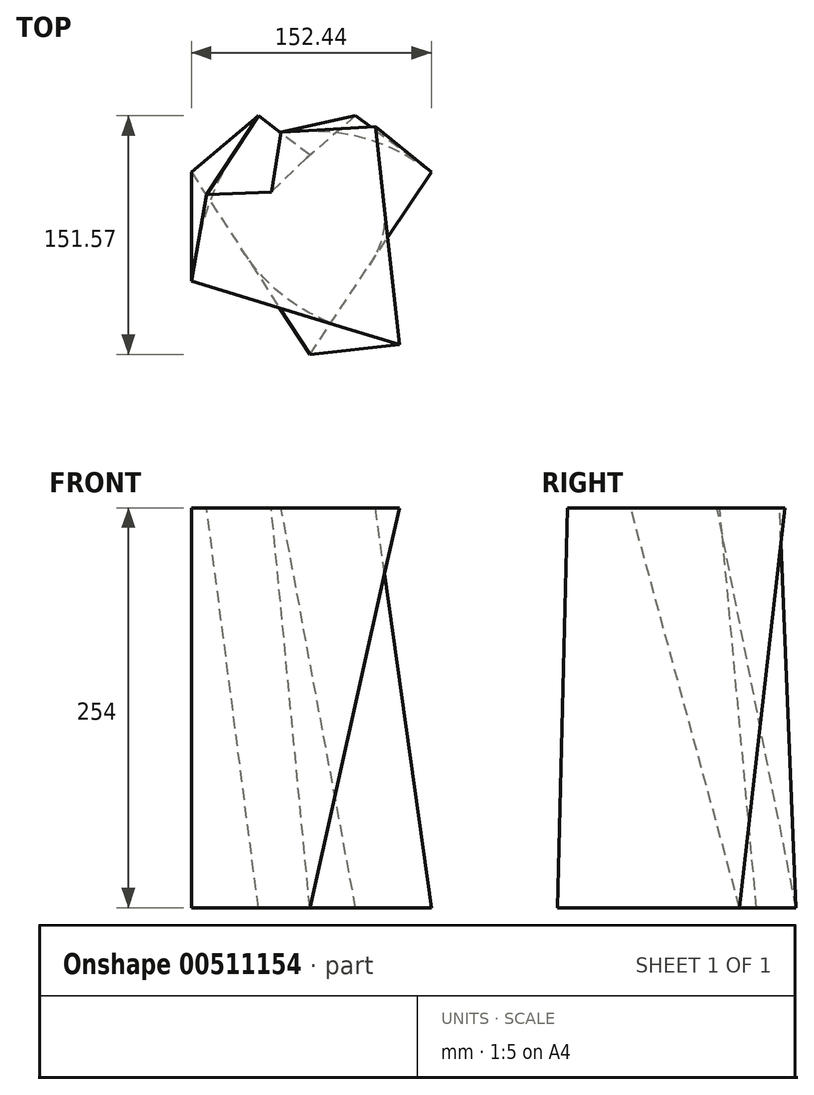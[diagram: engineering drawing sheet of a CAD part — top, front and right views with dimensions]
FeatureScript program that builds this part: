
annotation { "Feature Type Name" : "Feature", "Feature Type Description" : "" }
export const myFeature = defineFeature(function(context is Context, id is Id, definition is map)
    precondition{}
    {
        {
            var Q0;
            Q0=qCreatedBy(makeId("Top.planeOp"),FACE);
            var sketch = newSketch(context, id + "F0", { "sketchPlane" : qUnion([Q0])});
            skLineSegment(sketch, "E0", {"start": v(0, 50.57) * mm, "end": v(-32.65, 75.64) * mm});
            skLineSegment(sketch, "E1", {"start": v(-32.65, 75.64) * mm, "end": v(-75.2, 39.79) * mm});
            skLineSegment(sketch, "E2", {"start": v(-75.2, 39.79) * mm, "end": v(0, -75.93) * mm});
            skLineSegment(sketch, "E3", {"start": v(0, -75.93) * mm, "end": v(77.24, 39.79) * mm});
            skLineSegment(sketch, "E4", {"start": v(77.24, 39.79) * mm, "end": v(29.15, 75.64) * mm});
            skLineSegment(sketch, "E5", {"start": v(29.15, 75.64) * mm, "end": v(0, 50.57) * mm});
            skSolve(sketch);
        }
        {
            var Q0;
            Q0=qCreatedBy(makeId("Top.planeOp"),FACE);
            cPlane(context, id + "F1", {"entities" : qUnion([Q0]), "cplaneType" : CPlaneType.OFFSET, "offset" : 254 * mm, "width" : 152.4 * mm, "height" : 152.4 * mm});
        }
        {
            var Q0;
            Q0=qCreatedBy(id+"F1.planeOp",FACE);
            var sketch = newSketch(context, id + "F2", { "sketchPlane" : qUnion([Q0])});
            skLineSegment(sketch, "E6", {"start": v(-24.42, 27.24) * mm, "end": v(-65.55, 25.46) * mm});
            skLineSegment(sketch, "E7", {"start": v(-65.55, 25.46) * mm, "end": v(-75.1, -29.36) * mm});
            skLineSegment(sketch, "E8", {"start": v(-75.1, -29.36) * mm, "end": v(56.89, -69.67) * mm});
            skLineSegment(sketch, "E9", {"start": v(56.89, -69.67) * mm, "end": v(41.68, 68.63) * mm});
            skLineSegment(sketch, "E10", {"start": v(41.68, 68.63) * mm, "end": v(-18.2, 65.18) * mm});
            skLineSegment(sketch, "E11", {"start": v(-18.2, 65.18) * mm, "end": v(-24.42, 27.24) * mm});
            skLineSegment(sketch, "E12.0", {"start": v(-65.55, 25.46) * mm, "end": v(-18.2, 65.18) * mm, "construction": true});
            skLineSegment(sketch, "E13.0", {"start": v(-75.1, -29.36) * mm, "end": v(41.68, 68.63) * mm, "construction": true});
            skSolve(sketch);
        }
        {
            var Q0;
            Q0=makeQuery(id+"F0.imprint","IMPRINT",FACE,{"disambiguationData":[TD([[makeQuery(id+"F0.imprint","IMPRINT",EDGE,{"derivedFrom":sQuery(id+"F0.wireOp",EDGE,"E0")}),1.0]])]});
            var Q1;
            Q1=makeQuery(id+"F2.imprint","IMPRINT",FACE,{"disambiguationData":[TD([[makeQuery(id+"F2.imprint","IMPRINT",EDGE,{"derivedFrom":sQuery(id+"F2.wireOp",EDGE,"E6")}),1.0]])]});
            loft(context, id + "F3", {"sheetProfilesArray" : [{ "sheetProfileEntities" : qUnion([Q0]) }, { "sheetProfileEntities" : qUnion([Q1]) }]});
        }
    });
